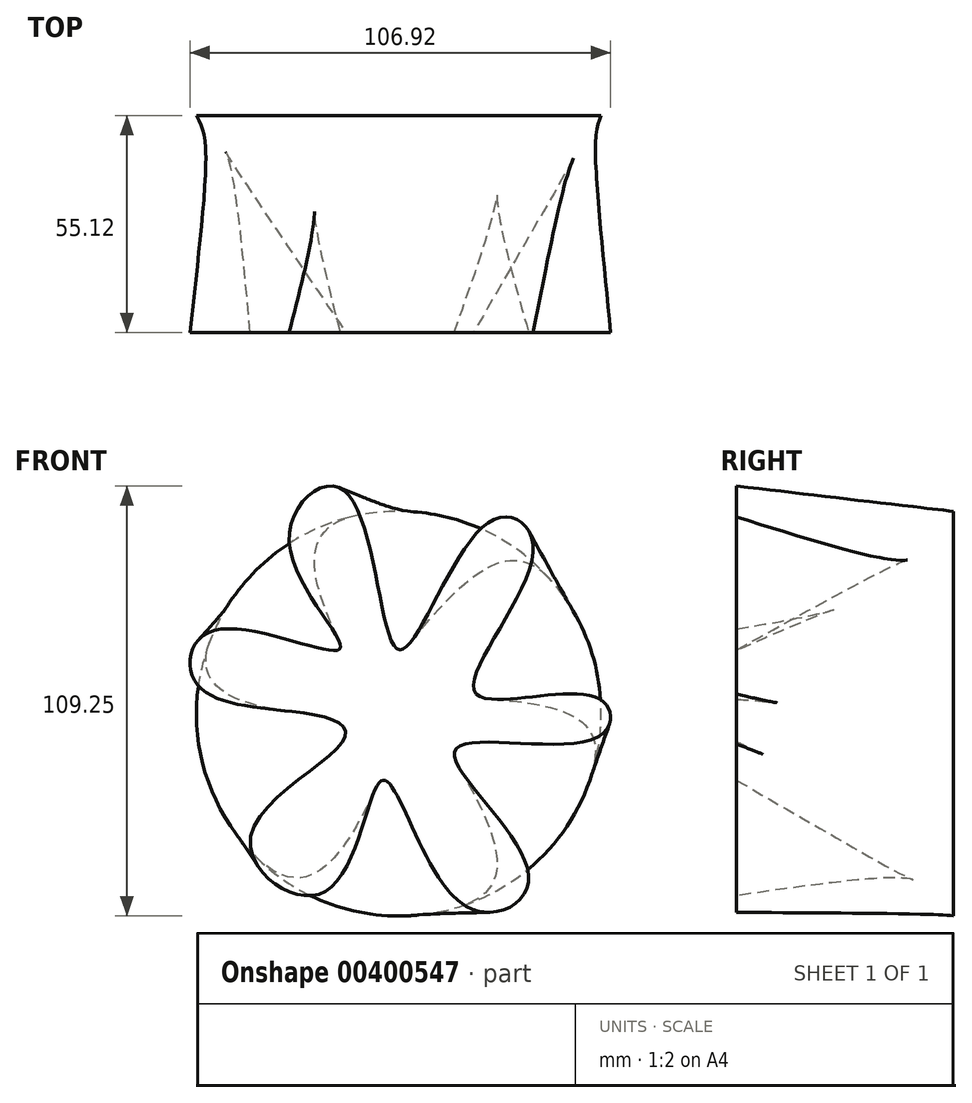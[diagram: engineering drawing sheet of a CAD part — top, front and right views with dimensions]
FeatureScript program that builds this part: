
annotation { "Feature Type Name" : "Feature", "Feature Type Description" : "" }
export const myFeature = defineFeature(function(context is Context, id is Id, definition is map)
    precondition{}
    {
        {
            var Q0;
            Q0=qCreatedBy(makeId("Front.planeOp"),FACE);
            cPlane(context, id + "F0", {"entities" : qUnion([Q0]), "cplaneType" : CPlaneType.OFFSET, "offset" : 55.12 * mm, "width" : 152.4 * mm, "height" : 152.4 * mm});
        }
        {
            var Q0;
            Q0=qCreatedBy(makeId("Front.planeOp"),FACE);
            var sketch = newSketch(context, id + "F1", { "sketchPlane" : qUnion([Q0])});
            skCircle(sketch, "E0", {"center": v(0, 0) * mm, "radius": 51.41 * mm});
            skSolve(sketch);
        }
        {
            var Q0;
            Q0=qCreatedBy(id+"F0.planeOp",FACE);
            var sketch = newSketch(context, id + "F2", { "sketchPlane" : qUnion([Q0])});
            skFitSpline(sketch, "E1", {"points": [v(-27.84, 44.1) * mm, v(-13.96, 56.72) * mm, v(0, 16.26) * mm, v(23.04, 48.72) * mm, v(34.14, 41.6) * mm, v(19.45, 5.28) * mm, v(50.58, 3.92) * mm, v(50.6, -5.93) * mm, v(14.3, -9.27) * mm, v(32.97, -41.27) * mm, v(16.73, -48.7) * mm, v(-3.99, -16.92) * mm, v(-18.76, -45.2) * mm, v(-37.72, -32.17) * mm, v(-13.88, -6.56) * mm, v(-19.52, -0.7) * mm, v(-50.98, 7.14) * mm, v(-47.3, 21.02) * mm, v(-15.05, 16.4) * mm, v(-27.84, 44.1) * mm]});
            skSolve(sketch);
        }
        {
            var Q0;
            Q0 = qSketchRegion(id + "F1", true);
            var Q1;
            Q1 = qSketchRegion(id + "F2", true);
            loft(context, id + "F3", {"sheetProfilesArray" : [{ "sheetProfileEntities" : qUnion([Q0]) }, { "sheetProfileEntities" : qUnion([Q1]) }]});
        }
    });
